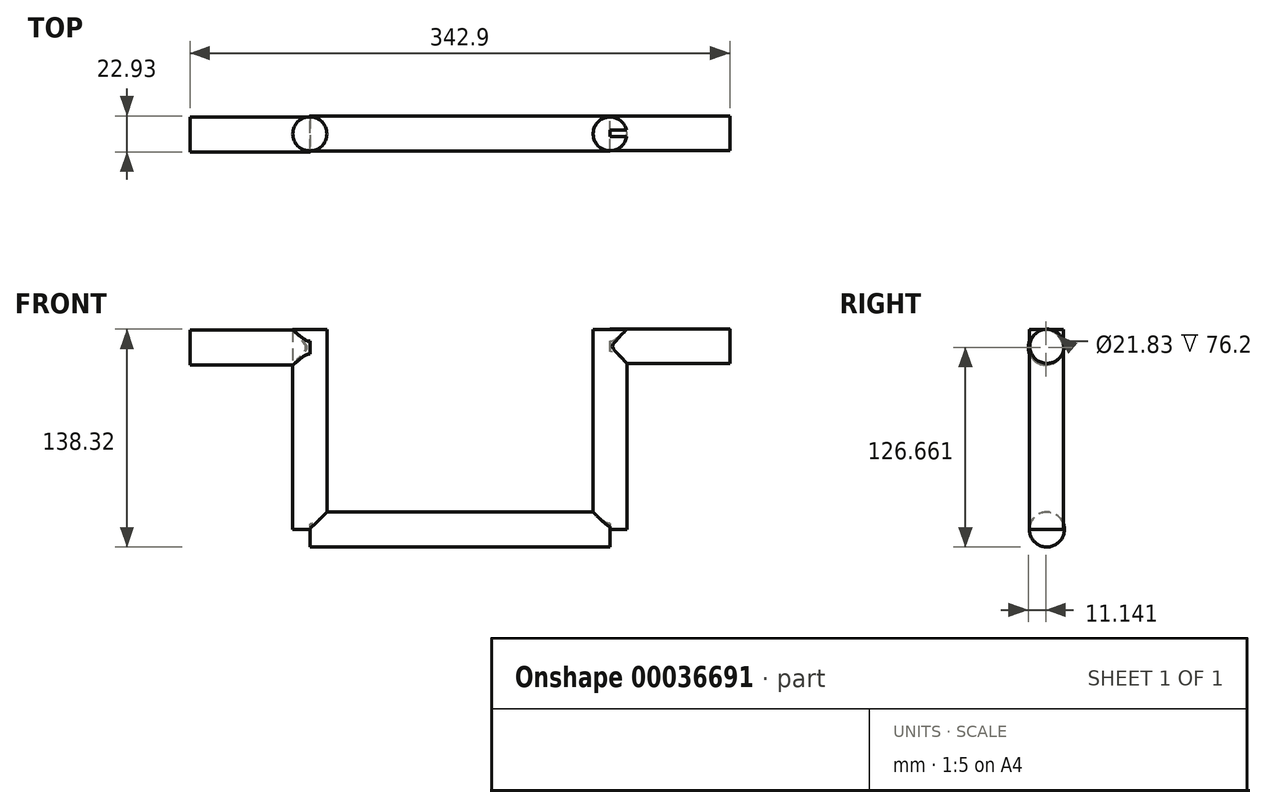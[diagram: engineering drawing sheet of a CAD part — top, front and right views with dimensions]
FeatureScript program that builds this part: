
annotation { "Feature Type Name" : "Feature", "Feature Type Description" : "" }
export const myFeature = defineFeature(function(context is Context, id is Id, definition is map)
    precondition{}
    {
        {
            var Q0;
            Q0=qCreatedBy(makeId("Right.planeOp"),FACE);
            var sketch = newSketch(context, id + "F0", { "sketchPlane" : qUnion([Q0])});
            skArc(sketch, "E0", {"start": v(-68.59, -8.12) * mm, "mid": v(-66.6, 5.64) * mm, "end": v(-79.6, 10.57) * mm});
            skArc(sketch, "E1", {"start": v(-79.6, 10.57) * mm, "mid": v(-85.75, -5.64) * mm, "end": v(-68.59, -8.12) * mm});
            skSolve(sketch);
        }
        {
            var Q0;
            Q0 = qSketchRegion(id + "F0", true);
            extrude(context, id + "F1", {"entities" : qUnion([Q0]), "depth" : 190.5 * mm});
        }
        {
            var Q0;
            Q0=qCreatedBy(makeId("Top.planeOp"),FACE);
            var sketch = newSketch(context, id + "F2", { "sketchPlane" : qUnion([Q0])});
            skCircle(sketch, "E2", {"center": v(0, -76.42) * mm, "radius": 10.82 * mm});
            skCircle(sketch, "E3", {"center": v(190.62, -76.42) * mm, "radius": 10.7 * mm});
            skSolve(sketch);
        }
        {
            var Q0;
            Q0=makeQuery(id+"F2.imprint","IMPRINT",FACE,{"disambiguationData":[TD([[makeQuery(id+"F2.imprint","IMPRINT",EDGE,{"derivedFrom":sQuery(id+"F2.wireOp",EDGE,"E2")}),1.0]])]});
            extrude(context, id + "F3", {"entities" : qUnion([Q0]), "operationType" : NewBodyOperationType.ADD, "depth" : 127 * mm});
        }
        {
            var Q0;
            Q0 = qSketchRegion(id + "F2", true);
            extrude(context, id + "F4", {"entities" : qUnion([Q0]), "operationType" : NewBodyOperationType.ADD, "depth" : 127 * mm});
        }
        {
            var Q0;
            Q0=qCreatedBy(makeId("Right.planeOp"),FACE);
            var sketch = newSketch(context, id + "F5", { "sketchPlane" : qUnion([Q0])});
            skCircle(sketch, "E4", {"center": v(-76.85, 115.55) * mm, "radius": 11.14 * mm});
            skCircle(sketch, "E5", {"center": v(-76.85, 115.55) * mm, "radius": 11.44 * mm});
            skCircle(sketch, "E6", {"center": v(-76.85, 115.55) * mm, "radius": 10.92 * mm});
            skSolve(sketch);
        }
        {
            var Q0;
            Q0=makeQuery(id+"F5.imprint","IMPRINT",FACE,{"disambiguationData":[TD([[makeQuery(id+"F5.imprint","IMPRINT",EDGE,{"derivedFrom":sQuery(id+"F5.wireOp",EDGE,"E4")}),1.0]])]});
            extrude(context, id + "F6", {"entities" : qUnion([Q0]), "operationType" : NewBodyOperationType.ADD, "oppositeDirection" : true, "depth" : 76.2 * mm});
        }
        {
            var Q0;
            Q0=makeQuery(id+"F1.opExtrude","CAP_FACE",FACE,{"disambiguationData":[OSD([sQuery(id+"F0.wireOp",EDGE,"E0"),sQuery(id+"F0.wireOp",EDGE,"E1")])],"isStart":false});
            var sketch = newSketch(context, id + "F7", { "sketchPlane" : qUnion([Q0])});
            skCircle(sketch, "E7", {"center": v(-76.12, 116.33) * mm, "radius": 10.88 * mm});
            skSolve(sketch);
        }
        {
            var Q0;
            Q0 = qSketchRegion(id + "F7", true);
            extrude(context, id + "F8", {"entities" : qUnion([Q0]), "operationType" : NewBodyOperationType.ADD, "depth" : 76.2 * mm});
        }
    });
